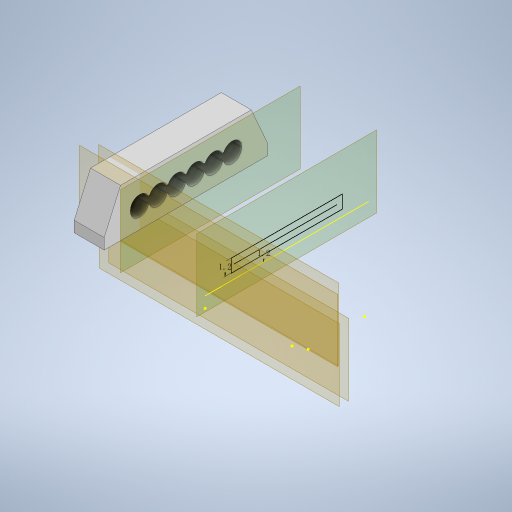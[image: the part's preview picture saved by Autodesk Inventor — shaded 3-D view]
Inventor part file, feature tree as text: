
AUTODESK INVENTOR PART (.ipt)
format: ipt  version: 2023 (Build 270158000, 158)  size: 460,288 bytes
history: native  units: mm
features: sketch x13, extrude x7, plane x6, loft x1
ambient origin geometry x8: Origin, YZ Plane, XZ Plane, XY Plane, X Axis, Y Axis, Z Axis, Center Point
bodies: 实体1 (feature_tree)
feature tree (27):
  extrude  "拉伸1"  Depth=20.0mm
  sketch  "草图2"  dims[d3=1.0mm d4=0.0mm d5=-1.5mm]
  plane  "工作平面1"
  extrude  "拉伸2"  [1 undecoded]
  extrude  "拉伸3"  Depth=12.0mm
  plane  "工作平面3"
  sketch  "草图6"  dims[d13=12.0mm d14=0.0mm d39=0.85mm]
  extrude  "拉伸5"  Depth=12.0mm TaperAngle=0.0deg
  sketch  "草图8"  dims[d44=-5.0mm d54=1.7mm]
  plane  "工作平面4"
  plane  "工作平面5"
  sketch  "草图10"  dims[d56=60.0mm d58=1.7mm d59=10.0mm d61=10.0mm d63=7.5mm]
  plane  "工作平面6"
  loft  "放样1"
  extrude  "拉伸6"  TaperAngle=0.0deg  [1 undecoded]
  extrude  "拉伸7"  Depth=1.7mm
  sketch  "草图14"  dims[d74=2.4mm]
  extrude  "拉伸8"  Depth=10.0mm
  sketch  "草图1"  dims[d1=15.0mm d2=20.0mm]
  sketch  "草图3"  dims[d6=3.4mm d8=12.0mm]
  sketch  "草图4"  dims[d10=0.0mm d11=12.0mm d12=0.0mm]
  plane  "工作平面2"
  sketch  "草图7"  dims[d41=45.0deg d42=0.0mm d43=0.0mm]
  sketch  "草图11"  dims[d64=1.7mm]
  sketch  "草图12"  dims[d66=60.0mm d68=1.7mm d69=10.0mm d71=10.0mm]
  sketch  "草图13"  dims[d73=7.5mm]
  sketch  "草图15"  dims[d75=1.8mm d76=7.0mm d77=0.0mm d78=90.0deg d79=0.0mm d80=90.0deg d81=0.0mm d82=90.0deg d83=0.0mm d84=90.0deg d85=60.0mm d87=1.7mm d88=10.0mm d90=10.0mm d92=0.0mm d93=0.0mm d94=0.1mm d95=0.7mm d96=0.7mm d97=0.7mm d98=10.0mm d99=0.0mm d100=1.2mm d101=1.2mm d102=17.25mm d103=0.0mm]
note: 2 required parameter values undecoded (feature->parameter linkage not recoverable at this tier; creation-order binding heuristic only, values carry confidence <= 0.55)
